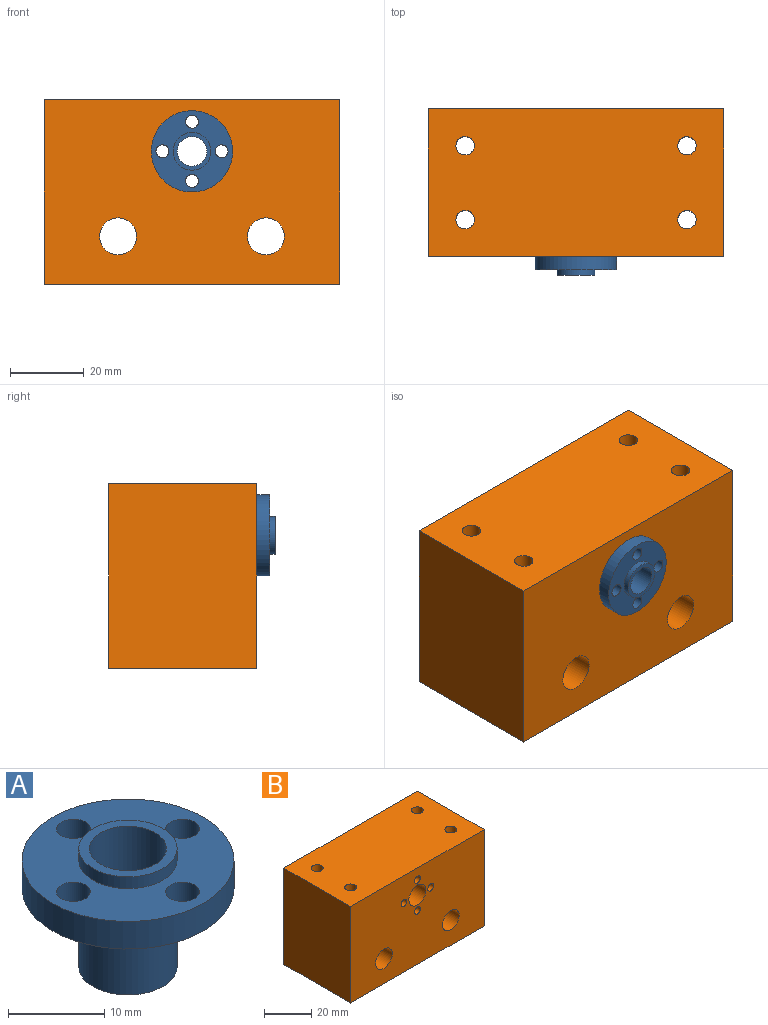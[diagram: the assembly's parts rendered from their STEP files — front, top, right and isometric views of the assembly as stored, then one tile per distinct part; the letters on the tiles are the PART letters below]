
ASSEMBLY  parts=2 mates=1
PART A: 12 faces, bbox 22x22x15 mm
  f0: plane 22x22mm, normal (0,0,-1), area 259.9mm2, adj f1,f7,f8,f9,f10,f11
  f1: cylinder r=5.1mm len=10.2mm, axis (0,0,-1), area 320.4mm2, adj f0,f2
  f2: plane 10.2x10.2mm, normal (0,0,-1), area 31.4mm2, adj f1,f3
  f3: cylinder r=4mm len=15mm, axis (0,0,-1), area 377mm2, adj f2,f4
  f4: plane 10.2x10.2mm, normal (0,0,1), area 31.4mm2, adj f3,f5
  f5: cylinder r=5.1mm len=10.2mm, axis (0,0,-1), area 48.1mm2, adj f4,f6
  f6: plane 22x22mm, normal (0,0,1), area 259.9mm2, adj f5,f7,f8,f9,f10,f11
  f7: cylinder r=11mm len=22mm, axis (0,0,-1), area 241.9mm2, adj f0,f6
  f8: cylinder r=1.75mm len=3.5mm, axis (0,0,1), area 38.5mm2, adj f0,f6
  f9: cylinder r=1.75mm len=3.5mm, axis (0,0,1), area 38.5mm2, adj f0,f6
  f10: cylinder r=1.75mm len=3.5mm, axis (0,0,1), area 38.5mm2, adj f0,f6
  f11: cylinder r=1.75mm len=3.5mm, axis (0,0,1), area 38.5mm2, adj f0,f6
PART B: 17 faces, bbox 80x40x50 mm
  f0: plane 80x40mm, normal (0,0,-1), area 3121.5mm2, adj f2,f3,f11,f12,f13,f14,f15,f16
  f1: plane 80x40mm, normal (0,0,1), area 3121.5mm2, adj f2,f3,f11,f12,f13,f14,f15,f16
  f2: plane 50x40mm, normal (-1,0,0), area 2000mm2, adj f0,f1,f11,f12
  f3: plane 50x40mm, normal (1,0,0), area 2000mm2, adj f0,f1,f11,f12
  f4: cylinder r=5mm len=40mm, axis (0,1,0), area 1256.6mm2, adj f11,f12
  f5: cylinder r=1.75mm len=40mm, axis (0,1,0), area 439.8mm2, adj f11,f12
  f6: cylinder r=1.75mm len=40mm, axis (0,1,0), area 439.8mm2, adj f11,f12
  f7: cylinder r=1.75mm len=40mm, axis (0,1,0), area 439.8mm2, adj f11,f12
  f8: cylinder r=1.75mm len=40mm, axis (0,1,0), area 439.8mm2, adj f11,f12
  f9: cylinder r=5.1mm len=40mm, axis (0,1,0), area 1281.8mm2, adj f11,f12
  f10: cylinder r=5mm len=40mm, axis (0,1,0), area 1256.6mm2, adj f11,f12
  f11: plane 80x50mm, normal (0,-1,0), area 3722.7mm2, adj f0,f1,f2,f3,f4,f5,f6,f7
  f12: plane 80x50mm, normal (0,1,0), area 3722.7mm2, adj f0,f1,f2,f3,f4,f5,f6,f7
  f13: cylinder r=2.5mm len=50mm, axis (0,0,1), area 785.4mm2, adj f0,f1
  f14: cylinder r=2.5mm len=50mm, axis (0,0,1), area 785.4mm2, adj f0,f1
  f15: cylinder r=2.5mm len=50mm, axis (0,0,1), area 785.4mm2, adj f0,f1
  f16: cylinder r=2.5mm len=50mm, axis (0,0,1), area 785.4mm2, adj f0,f1
PLACE A rot(axis=(1,0,0),90deg) t=(-19.58,-15.17,19.67)mm
PLACE B t=(-19.58,17.33,3.67)mm
MATE fastened A.f10 <-> B.f8  axis (0,1,0) through (-19.58,-22.67,27.67)mm
